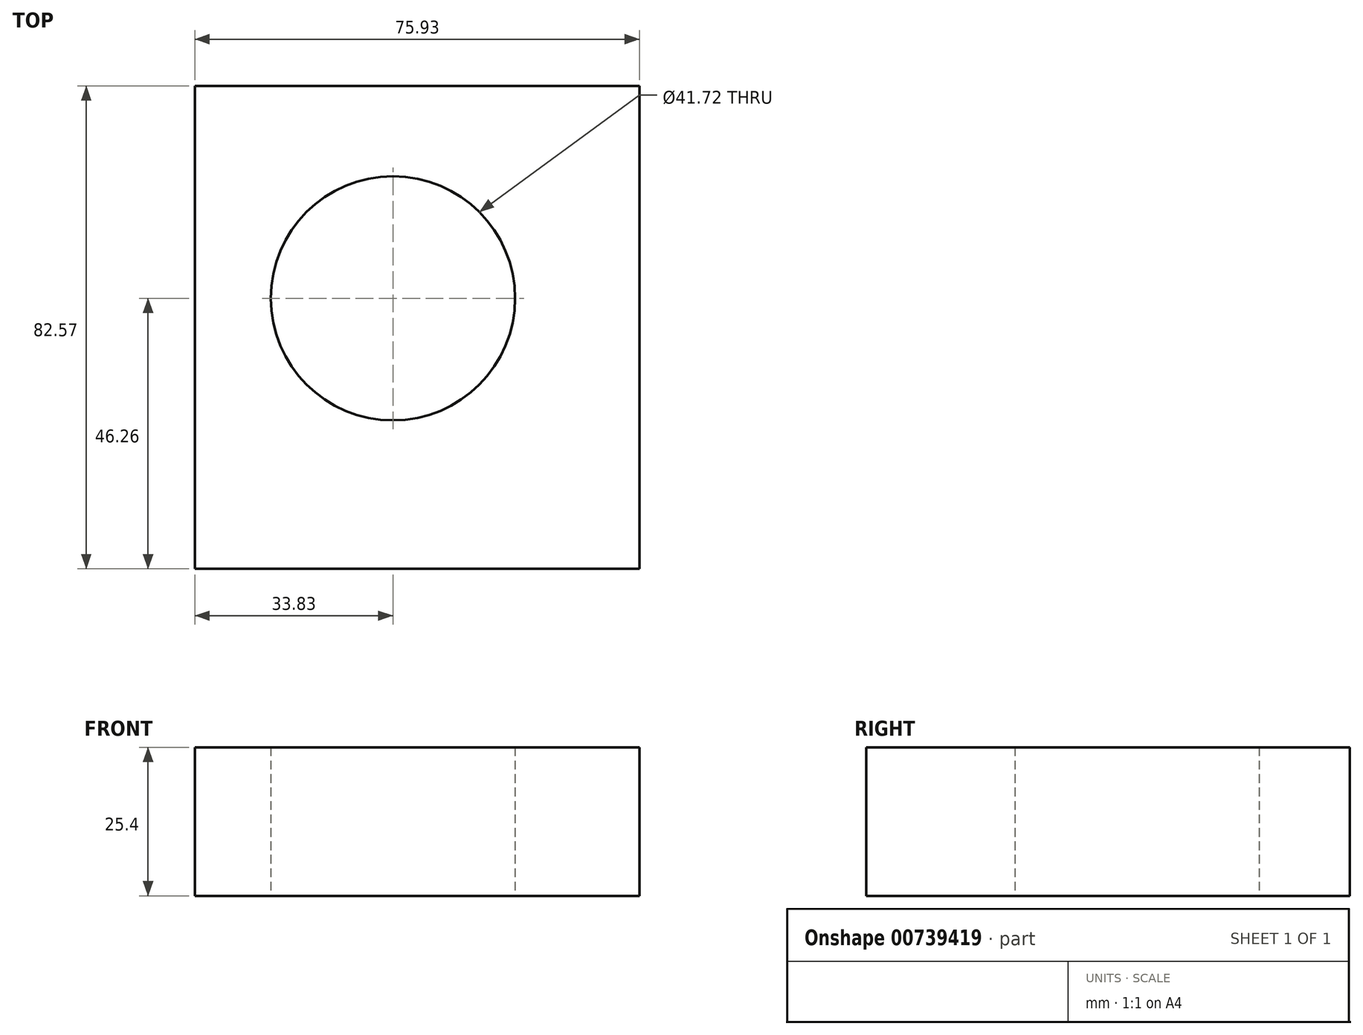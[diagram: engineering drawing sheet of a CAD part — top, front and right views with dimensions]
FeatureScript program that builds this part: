
annotation { "Feature Type Name" : "Feature", "Feature Type Description" : "" }
export const myFeature = defineFeature(function(context is Context, id is Id, definition is map)
    precondition{}
    {
        {
            var Q0;
            Q0=qCreatedBy(makeId("Top.planeOp"),FACE);
            var sketch = newSketch(context, id + "F0", { "sketchPlane" : qUnion([Q0])});
            skLineSegment(sketch, "E0.bottom", {"start": v(30.9, 36.3) * mm, "end": v(-45.03, 36.3) * mm});
            skLineSegment(sketch, "E0.top", {"start": v(30.9, -46.26) * mm, "end": v(-45.03, -46.26) * mm});
            skLineSegment(sketch, "E0.left", {"start": v(30.9, 36.3) * mm, "end": v(30.9, -46.26) * mm});
            skLineSegment(sketch, "E0.right", {"start": v(-45.03, 36.3) * mm, "end": v(-45.03, -46.26) * mm});
            skSolve(sketch);
        }
        {
            var Q0;
            Q0=makeQuery(id+"F0.imprint","IMPRINT",FACE,{"disambiguationData":[TD([[makeQuery(id+"F0.imprint","IMPRINT",EDGE,{"derivedFrom":sQuery(id+"F0.wireOp",EDGE,"E0.bottom")}),1.0]])]});
            var sketch = newSketch(context, id + "F1", { "sketchPlane" : qUnion([Q0])});
            skCircle(sketch, "E1", {"center": v(-11.2, 0) * mm, "radius": 20.86 * mm});
            skSolve(sketch);
        }
        {
            var Q0;
            Q0=makeQuery(id+"F1.imprint","IMPRINT",FACE,{"disambiguationData":[TD([[makeQuery(id+"F1.imprint","IMPRINT",EDGE,{"derivedFrom":sQuery(id+"F1.wireOp",EDGE,"E1")}),-1.0]])]});
            extrude(context, id + "F2", {"entities" : qUnion([Q0]), "depth" : 25.4 * mm, "offsetDistance" : 25.4 * mm});
        }
        {
            var Q0;
            Q0=makeQuery(id+"F0.imprint","IMPRINT",FACE,{"disambiguationData":[TD([[makeQuery(id+"F0.imprint","IMPRINT",EDGE,{"derivedFrom":sQuery(id+"F0.wireOp",EDGE,"E0.bottom")}),1.0]])]});
            var sketch = newSketch(context, id + "F3", { "sketchPlane" : qUnion([Q0])});
            skCircle(sketch, "E2", {"center": v(-11.68, 0) * mm, "radius": 17 * mm});
            skSolve(sketch);
        }
        {
            var Q0;
            Q0=sQuery(id+"F3.wireOp",EDGE,"E2");
            extrude(context, id + "F4", {"bodyType" : ToolBodyType.SURFACE, "surfaceEntities" : qUnion([Q0]), "depth" : 152.4 * mm, "offsetDistance" : 25.4 * mm});
        }
    });
